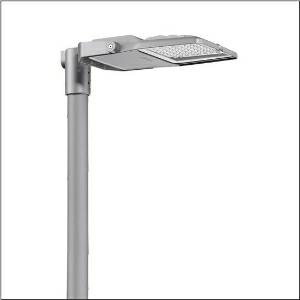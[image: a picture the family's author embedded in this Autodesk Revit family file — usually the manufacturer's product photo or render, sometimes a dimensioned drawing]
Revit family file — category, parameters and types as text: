
# Revit family: floodlight_fl_21_iq_mini___pl52_5xa7772d4d3a_25ab
name_source: partatom
category: Lighting Fixtures
units: mm (PartAtom-declared; Revit-internal decimal feet)

## family parameters
Cut with Voids When Loaded = No
Host = Face
Light Source = No
Part Type = Normal
Room Calculation Point = No
Round Connector Dimension = Use Diameter
Shared = No

## types (1)
- --- (1 x LED, 18610 lm, 143 W, 4000K)
    Apparent Load = 143 VA
    CIE Flux Codes = 26 60 98 100 100
    Color Rendering = 70
    Color Temperature = 4000K
    Default Elevation = 1800 mm
    Description = Floodlight FL 21 iQ mini, floodlight, primary light control with lens, of PMMA, primary optical cover: protective disc, of toughened safety glass, transparent, light distribution: PL52, light emission: direct distribution, installation type: surface-mounted, LED, High Power LED, rated luminous flux: 18.610lm, luminous efficacy: 130lm/W, light colour: 740, colour temperature: 4000K, control gear: iQ Street-Remote/DALI, control: Auto-Match, Temp-Guard, Night-Set, Smart-Wire, Desk-Remote (wireless, voltage-free reading and setting of iQ features in the workshop via application-optimized NFC function/RFID function), optimised constant luminous flux control (CLO 2.0), Light-Fading, Lumen-Switch, with terminal, 6-pole, mains connection: 220..240V, AC, 50/60Hz, start of lifetime: 143W, end of service life: 152W, reduction: 61W, luminaire housing, of diecast aluminium, powder-coated, Siteco® metallic grey (DB 702S), corrosivity category C5 mid according to DIN EN ISO 12944, suitable for swimming pools, chlorine-resistant, sealing non-destructively replaceable, please order mast flange separately, mast bracket, of steel, galvanised, powder-coated, protection rating (complete): IP66, insulation class (complete): insulation class II (safety insulation), certification: CE, ENEC, VDE, protection symbol: D, impact resistance: IK08, permissible operating ambient temperature: -40..+40°C, permissible operating ambient temperature for outdoor applications: -40..+50°C, standard: DIN EN 12944, LABS conformity tested according to VDMA 24364:2018-05, packaging unit: 1 piece

Light Distribution: PL52
    Height = 70 mm
    Lamp = 1 x LED
    Lamp Light Flux = 18610 lm
    Lamp Power = 143 W
    Lamp count = 1
    Length = 485 mm
    Luminous efficacy = 130 lm/W
    Manufacturer = Siteco
    ModVariant = No
    Model = 5XA7772D4D3A
    Number of Poles = 1
    OnlyDefault = Yes
    Power Factor = 1
    Product Name = Floodlight FL 21 iQ mini | PL52
    Product group = floodlight | pylon annexe
    ProductGroupID = 6200
    Protection Class = Protection class II
    Protection Degree = IP 66
    RLX_Detail_Level = 1
    RLX_Emergency_Light_Flux = 0 lm
    RLX_Emergency_Type = 0
    RLX_Emergency_Type_DB = No
    RlxData = <blob elided: 101881 chars, md5=ee66499d>
    Socket = socket
    Standby Power = 0 W
    System Light Flux = 18610 lm
    System Power = 143 W
    Type Comments = factory setting: luminous flux: 100 % | dim-lin: 254 | 730 mA
    Type Image = l_1007125.jpg
    URL = http://relux.com
    VarID = @adj_163560
    Voltage = 0 V
    Weight = 0.00 kg
    Width = 337 mm

## geometry (parser evidence)
native form markers: Blend x4, Sweep x12
no freeform markers — native parametric forms only
